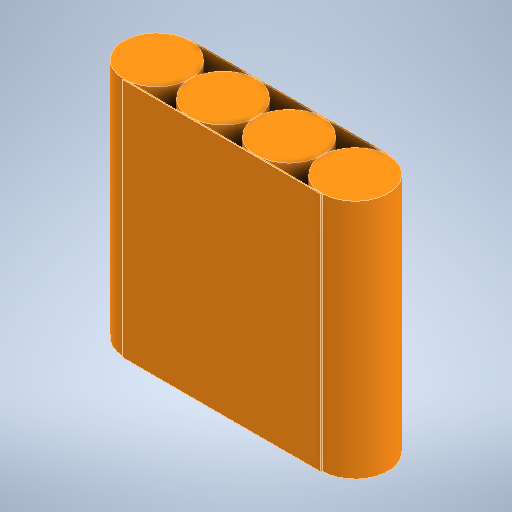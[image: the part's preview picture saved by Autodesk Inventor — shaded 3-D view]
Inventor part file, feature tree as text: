
AUTODESK INVENTOR PART (.ipt)
format: ipt  version: 2025.3 (Build 293356000, 356)  size: 245,248 bytes
history: native  units: mm
features: other x2, extrude x2, sketch x2, mirror x1
ambient origin geometry x8: Origin, YZ Plane, XZ Plane, XY Plane, X Axis, Y Axis, Z Axis, Center Point
bodies: Body1 (feature_tree)
feature tree (7):
  other  "ソリッド1"
  extrude  "押し出し1"  Depth=14.0mm
  other  "作業平面1"
  extrude  "押し出し2"  Depth=14.0mm
  mirror  "ミラー1"
  sketch  "スケッチ1"
  sketch  "スケッチ2"
